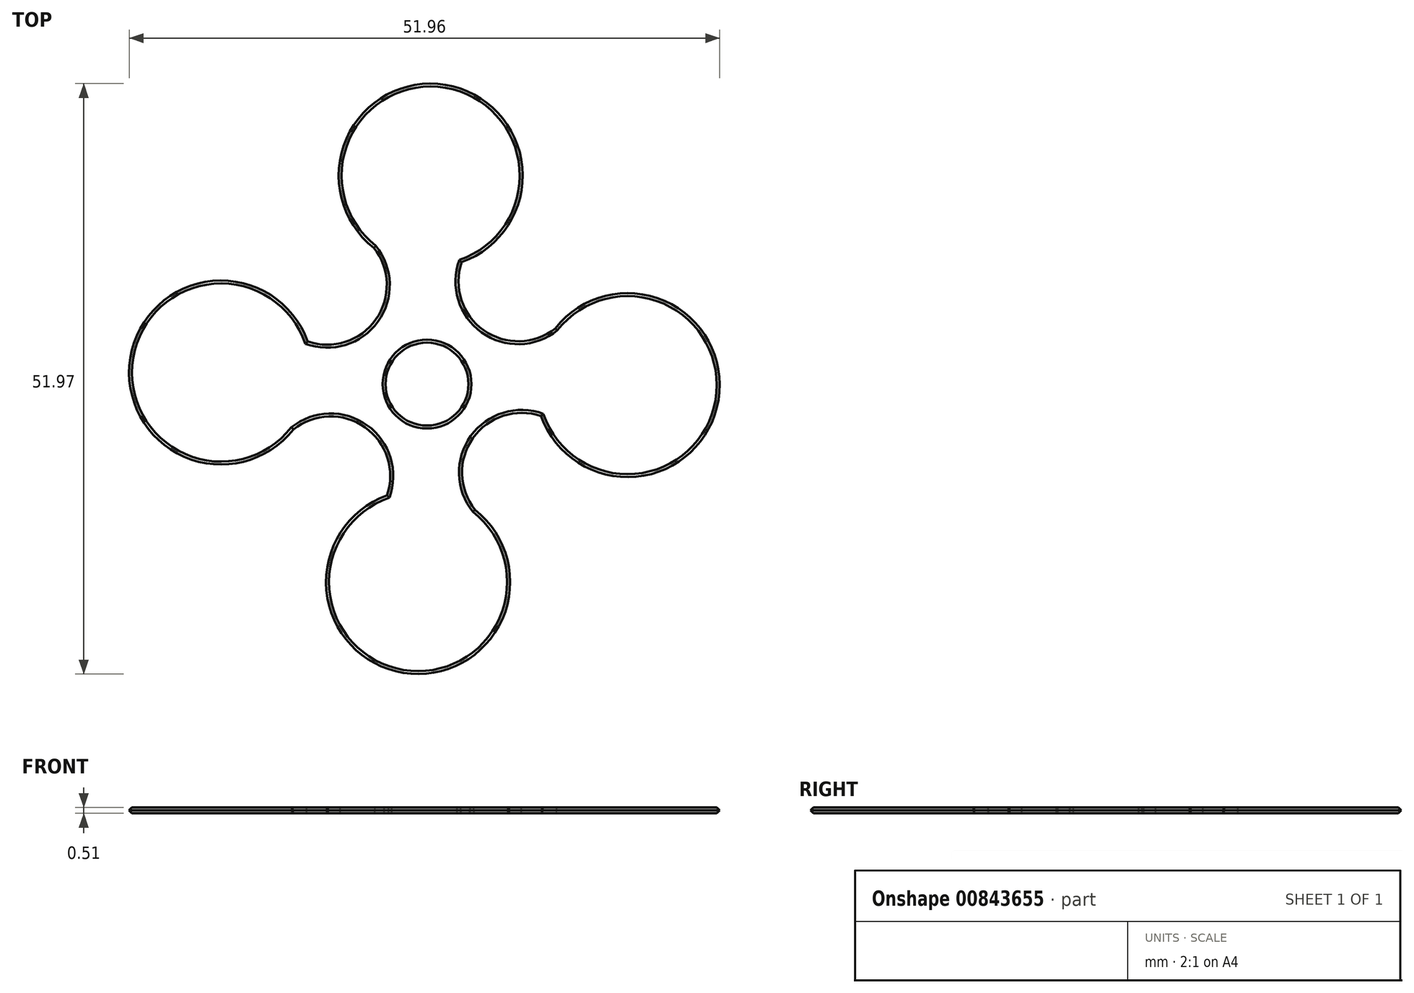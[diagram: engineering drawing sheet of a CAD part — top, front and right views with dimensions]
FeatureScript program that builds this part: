
annotation { "Feature Type Name" : "Feature", "Feature Type Description" : "" }
export const myFeature = defineFeature(function(context is Context, id is Id, definition is map)
    precondition{}
    {
        {
            var Q0;
            Q0=qCreatedBy(makeId("Top.planeOp"),FACE);
            var sketch = newSketch(context, id + "F0", { "sketchPlane" : qUnion([Q0])});
            skLineSegment(sketch, "E0.bottom", {"start": v(-3.95, -5.45) * mm, "end": v(-4.68, -5.45) * mm});
            skLineSegment(sketch, "E0.top", {"start": v(4.68, 5.45) * mm, "end": v(4.17, 5.45) * mm});
            skLineSegment(sketch, "E0.left", {"start": v(4.68, 4.97) * mm, "end": v(4.68, 5.45) * mm});
            skLineSegment(sketch, "E0.right", {"start": v(-4.68, -5.45) * mm, "end": v(-4.68, -4.47) * mm});
            skPoint(sketch, "E0.middle", {"position": v(0, 0) * mm});
            skCircle(sketch, "E1", {"center": v(0, 0) * mm, "radius": 3.65 * mm});
            skArc(sketch, "E2", {"start": v(-4.68, 11.99) * mm, "mid": v(-1.03, 10.04) * mm, "end": v(3.05, 10.73) * mm});
            skArc(sketch, "E3.1.0", {"start": v(-11.76, -3.98) * mm, "mid": v(-9.81, -0.33) * mm, "end": v(-10.5, 3.74) * mm});
            skArc(sketch, "E3.2.0", {"start": v(4.22, -11.06) * mm, "mid": v(0.57, -9.11) * mm, "end": v(-3.51, -9.8) * mm});
            skArc(sketch, "E3.3.0", {"start": v(11.3, 4.91) * mm, "mid": v(9.35, 1.26) * mm, "end": v(10.03, -2.81) * mm});
            skPoint(sketch, "E3.center", {"position": v(-0.23, 0.47) * mm});
            skArc(sketch, "E4", {"start": v(-10.5, 3.74) * mm, "mid": v(-4.5, 5.69) * mm, "end": v(-4.68, 11.99) * mm});
            skArc(sketch, "E5.1.0", {"start": v(-3.51, -9.8) * mm, "mid": v(-5.45, -3.8) * mm, "end": v(-11.76, -3.98) * mm});
            skArc(sketch, "E5.2.0", {"start": v(10.03, -2.81) * mm, "mid": v(4.03, -4.76) * mm, "end": v(4.22, -11.06) * mm});
            skArc(sketch, "E5.3.0", {"start": v(3.05, 10.73) * mm, "mid": v(4.99, 4.73) * mm, "end": v(11.3, 4.91) * mm});
            skArc(sketch, "E6", {"start": v(10.03, -2.81) * mm, "mid": v(25.64, -1.39) * mm, "end": v(11.3, 4.91) * mm});
            skArc(sketch, "E7.1.0", {"start": v(3.05, 10.73) * mm, "mid": v(1.62, 26.34) * mm, "end": v(-4.68, 11.99) * mm});
            skArc(sketch, "E7.2.0", {"start": v(-10.5, 3.74) * mm, "mid": v(-26.1, 2.32) * mm, "end": v(-11.76, -3.98) * mm});
            skArc(sketch, "E7.3.0", {"start": v(-3.51, -9.8) * mm, "mid": v(-2.09, -25.41) * mm, "end": v(4.22, -11.06) * mm});
            skPoint(sketch, "E8.orphan", {"position": v(-4.68, 5.45) * mm});
            skPoint(sketch, "E9.orphan", {"position": v(4.68, -5.45) * mm});
            skSolve(sketch);
        }
        {
            var Q0;
            Q0=makeQuery(id+"F0.imprint","IMPRINT",FACE,{"disambiguationData":[TD([[makeQuery(id+"F0.imprint","IMPRINT",EDGE,{"derivedFrom":sQuery(id+"F0.wireOp",EDGE,"E1")}),-1.0]])]});
            var Q1;
            Q1=makeQuery(id+"F0.imprint","IMPRINT",FACE,{"disambiguationData":[TD([[makeQuery(id+"F0.imprint","IMPRINT",EDGE,{"derivedFrom":sQuery(id+"F0.wireOp",EDGE,"E3.1.0")}),1.0]])]});
            var Q2;
            Q2=makeQuery(id+"F0.imprint","IMPRINT",FACE,{"disambiguationData":[TD([[makeQuery(id+"F0.imprint","IMPRINT",EDGE,{"derivedFrom":sQuery(id+"F0.wireOp",EDGE,"E3.2.0")}),1.0]])]});
            var Q3;
            Q3=makeQuery(id+"F0.imprint","IMPRINT",FACE,{"disambiguationData":[TD([[makeQuery(id+"F0.imprint","IMPRINT",EDGE,{"derivedFrom":sQuery(id+"F0.wireOp",EDGE,"E3.3.0")}),1.0]])]});
            var Q4;
            Q4=makeQuery(id+"F0.imprint","IMPRINT",FACE,{"disambiguationData":[TD([[makeQuery(id+"F0.imprint","IMPRINT",EDGE,{"derivedFrom":sQuery(id+"F0.wireOp",EDGE,"E2")}),1.0]])]});
            extrude(context, id + "F1", {"entities" : qUnion([Q0, Q1, Q2, Q3, Q4]), "depth" : 0.5 * mm, "offsetDistance" : 25.4 * mm});
        }
        {
            var Q0;
            Q0=makeQuery(id+"F1.opExtrude","CAP_EDGE",EDGE,{"disambiguationData":[OSD([sQuery(id+"F0.wireOp",EDGE,"E7.3.0")])],"isStart":false});
            var Q1;
            Q1=makeQuery(id+"F1.opExtrude","CAP_EDGE",EDGE,{"disambiguationData":[OSD([sQuery(id+"F0.wireOp",EDGE,"E5.2.0")])],"isStart":false});
            var Q2;
            Q2=makeQuery(id+"F1.opExtrude","CAP_EDGE",EDGE,{"disambiguationData":[OSD([sQuery(id+"F0.wireOp",EDGE,"E6")])],"isStart":false});
            var Q3;
            Q3=makeQuery(id+"F1.opExtrude","CAP_EDGE",EDGE,{"disambiguationData":[OSD([sQuery(id+"F0.wireOp",EDGE,"E5.3.0")])],"isStart":false});
            var Q4;
            Q4=makeQuery(id+"F1.opExtrude","CAP_EDGE",EDGE,{"disambiguationData":[OSD([sQuery(id+"F0.wireOp",EDGE,"E7.1.0")])],"isStart":false});
            var Q5;
            Q5=makeQuery(id+"F1.opExtrude","CAP_EDGE",EDGE,{"disambiguationData":[OSD([sQuery(id+"F0.wireOp",EDGE,"E4")])],"isStart":false});
            var Q6;
            Q6=makeQuery(id+"F1.opExtrude","CAP_EDGE",EDGE,{"disambiguationData":[OSD([sQuery(id+"F0.wireOp",EDGE,"E7.2.0")])],"isStart":false});
            var Q7;
            Q7=makeQuery(id+"F1.opExtrude","CAP_EDGE",EDGE,{"disambiguationData":[OSD([sQuery(id+"F0.wireOp",EDGE,"E5.1.0")])],"isStart":false});
            var Q8;
            Q8=makeQuery(id+"F1.opExtrude","CAP_EDGE",EDGE,{"disambiguationData":[OSD([sQuery(id+"F0.wireOp",EDGE,"E7.1.0")])],"isStart":true});
            var Q9;
            Q9=makeQuery(id+"F1.opExtrude","CAP_EDGE",EDGE,{"disambiguationData":[OSD([sQuery(id+"F0.wireOp",EDGE,"E5.3.0")])],"isStart":true});
            var Q10;
            Q10=makeQuery(id+"F1.opExtrude","CAP_FACE",FACE,{"disambiguationData":[OSD([sQuery(id+"F0.wireOp",EDGE,"E1"),sQuery(id+"F0.wireOp",EDGE,"E4"),sQuery(id+"F0.wireOp",EDGE,"E5.1.0"),sQuery(id+"F0.wireOp",EDGE,"E5.2.0"),sQuery(id+"F0.wireOp",EDGE,"E5.3.0"),sQuery(id+"F0.wireOp",EDGE,"E6"),sQuery(id+"F0.wireOp",EDGE,"E7.1.0"),sQuery(id+"F0.wireOp",EDGE,"E7.2.0"),sQuery(id+"F0.wireOp",EDGE,"E7.3.0")])],"isStart":true});
            var Q11;
            Q11=makeQuery(id+"F1.opExtrude","CAP_EDGE",EDGE,{"disambiguationData":[OSD([sQuery(id+"F0.wireOp",EDGE,"E5.2.0")])],"isStart":true});
            var Q12;
            Q12=makeQuery(id+"F1.opExtrude","CAP_EDGE",EDGE,{"disambiguationData":[OSD([sQuery(id+"F0.wireOp",EDGE,"E4")])],"isStart":true});
            var Q13;
            Q13=makeQuery(id+"F1.opExtrude","CAP_EDGE",EDGE,{"disambiguationData":[OSD([sQuery(id+"F0.wireOp",EDGE,"E7.2.0")])],"isStart":true});
            var Q14;
            Q14=makeQuery(id+"F1.opExtrude","CAP_EDGE",EDGE,{"disambiguationData":[OSD([sQuery(id+"F0.wireOp",EDGE,"E5.1.0")])],"isStart":true});
            var Q15;
            Q15=makeQuery(id+"F1.opExtrude","CAP_EDGE",EDGE,{"disambiguationData":[OSD([sQuery(id+"F0.wireOp",EDGE,"E7.3.0")])],"isStart":true});
            var Q16;
            Q16=makeQuery(id+"F1.opExtrude","CAP_EDGE",EDGE,{"disambiguationData":[OSD([sQuery(id+"F0.wireOp",EDGE,"E1")])],"isStart":true});
            var Q17;
            Q17=makeQuery(id+"F1.opExtrude","CAP_EDGE",EDGE,{"disambiguationData":[OSD([sQuery(id+"F0.wireOp",EDGE,"E1")])],"isStart":false});
            chamfer(context, id + "F2", {"entities" : qUnion([Q0, Q1, Q2, Q3, Q4, Q5, Q6, Q7, Q8, Q9, Q10, Q11, Q12, Q13, Q14, Q15, Q16, Q17]), "width" : 0.25 * mm, "tangentPropagation" : true});
        }
    });
